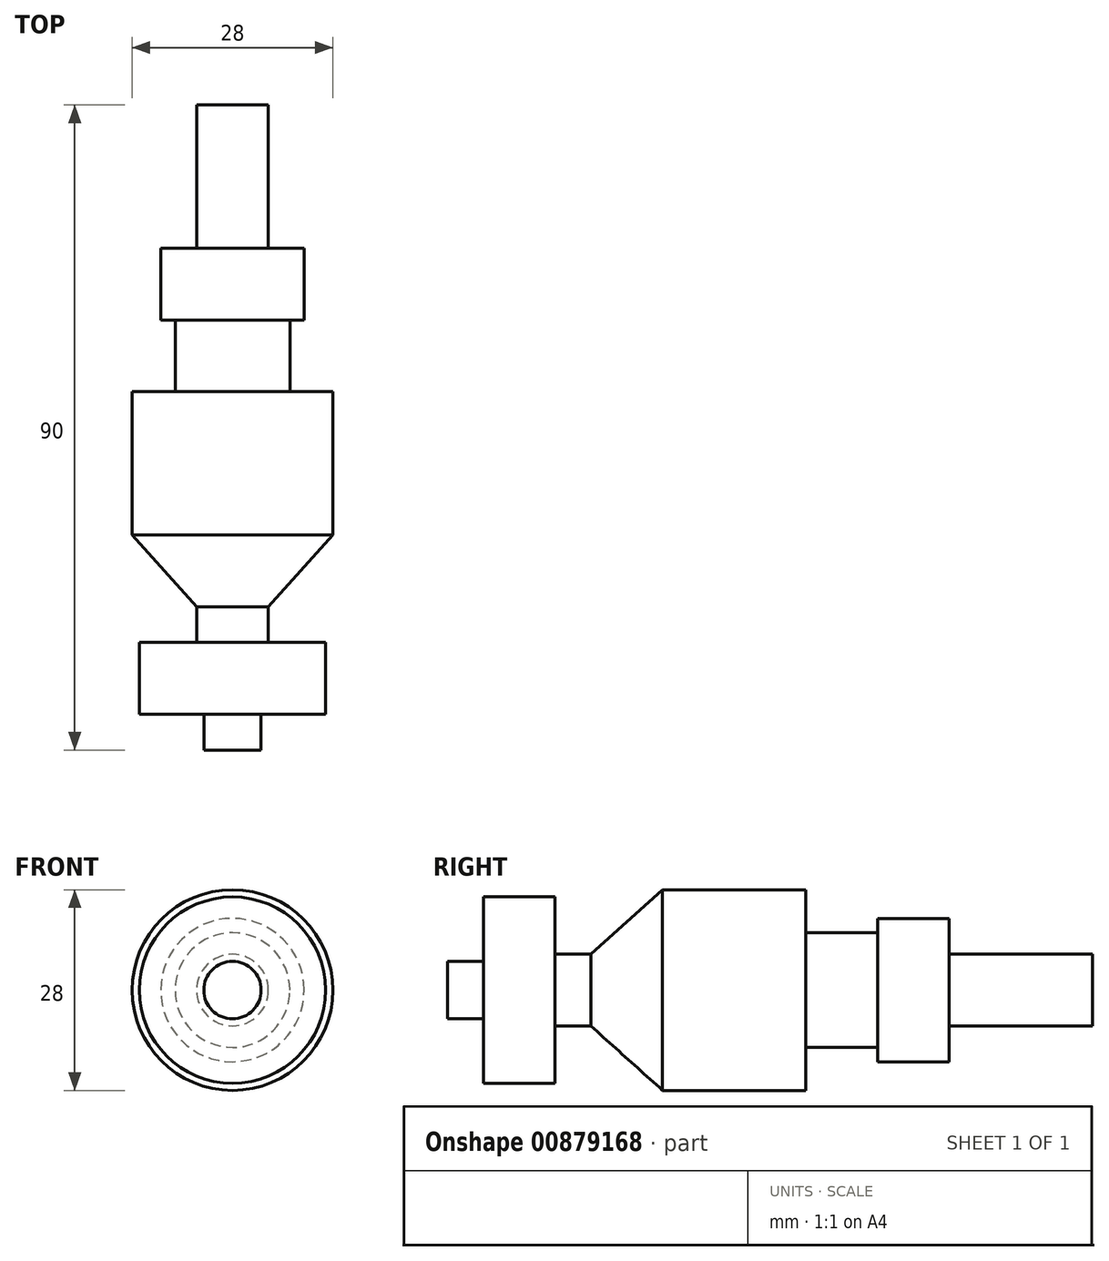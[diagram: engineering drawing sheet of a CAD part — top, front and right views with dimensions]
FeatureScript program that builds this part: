
annotation { "Feature Type Name" : "Feature", "Feature Type Description" : "" }
export const myFeature = defineFeature(function(context is Context, id is Id, definition is map)
    precondition{}
    {
        {
            var Q0;
            Q0=qCreatedBy(makeId("Right.planeOp"),FACE);
            var sketch = newSketch(context, id + "F0", { "sketchPlane" : qUnion([Q0])});
            skLineSegment(sketch, "E0", {"start": v(0, 0) * mm, "end": v(-56.54, 0) * mm, "construction": true});
            skLineSegment(sketch, "E1", {"start": v(0, 0) * mm, "end": v(0, 5) * mm});
            skLineSegment(sketch, "E2", {"start": v(0, 5) * mm, "end": v(-20, 5) * mm});
            skLineSegment(sketch, "E3", {"start": v(-20, 5) * mm, "end": v(-20, 10) * mm});
            skLineSegment(sketch, "E4", {"start": v(-20, 10) * mm, "end": v(-30, 10) * mm});
            skLineSegment(sketch, "E5", {"start": v(-30, 10) * mm, "end": v(-30, 8) * mm});
            skLineSegment(sketch, "E6", {"start": v(-30, 8) * mm, "end": v(-40, 8) * mm});
            skLineSegment(sketch, "E7", {"start": v(-40, 8) * mm, "end": v(-40, 14) * mm});
            skLineSegment(sketch, "E8", {"start": v(-40, 14) * mm, "end": v(-60, 14) * mm});
            skLineSegment(sketch, "E9", {"start": v(-60, 14) * mm, "end": v(-70, 5) * mm});
            skLineSegment(sketch, "E10", {"start": v(-70, 5) * mm, "end": v(-75, 5) * mm});
            skLineSegment(sketch, "E11", {"start": v(-75, 5) * mm, "end": v(-75, 13) * mm});
            skLineSegment(sketch, "E12", {"start": v(-75, 13) * mm, "end": v(-85, 13) * mm});
            skLineSegment(sketch, "E13", {"start": v(-85, 13) * mm, "end": v(-85, 4) * mm});
            skLineSegment(sketch, "E14", {"start": v(-85, 4) * mm, "end": v(-90, 4) * mm});
            skLineSegment(sketch, "E15", {"start": v(-90, 4) * mm, "end": v(-90, 0) * mm});
            skLineSegment(sketch, "E16", {"start": v(-90, 0) * mm, "end": v(0, 0) * mm});
            skSolve(sketch);
        }
        {
            var Q0;
            Q0=makeQuery(id+"F0.imprint","IMPRINT",FACE,{"disambiguationData":[TD([[makeQuery(id+"F0.imprint","IMPRINT",EDGE,{"derivedFrom":sQuery(id+"F0.wireOp",EDGE,"E1")}),1.0]])]});
            var Q1;
            Q1=sQuery(id+"F0.wireOp",EDGE,"E16");
            revolve(context, id + "F1", {"surfaceOperationType" : NewSurfaceOperationType.NEW, "entities" : qUnion([Q0]), "axis" : qUnion([Q1]), "revolveType" : RevolveType.FULL});
        }
    });
